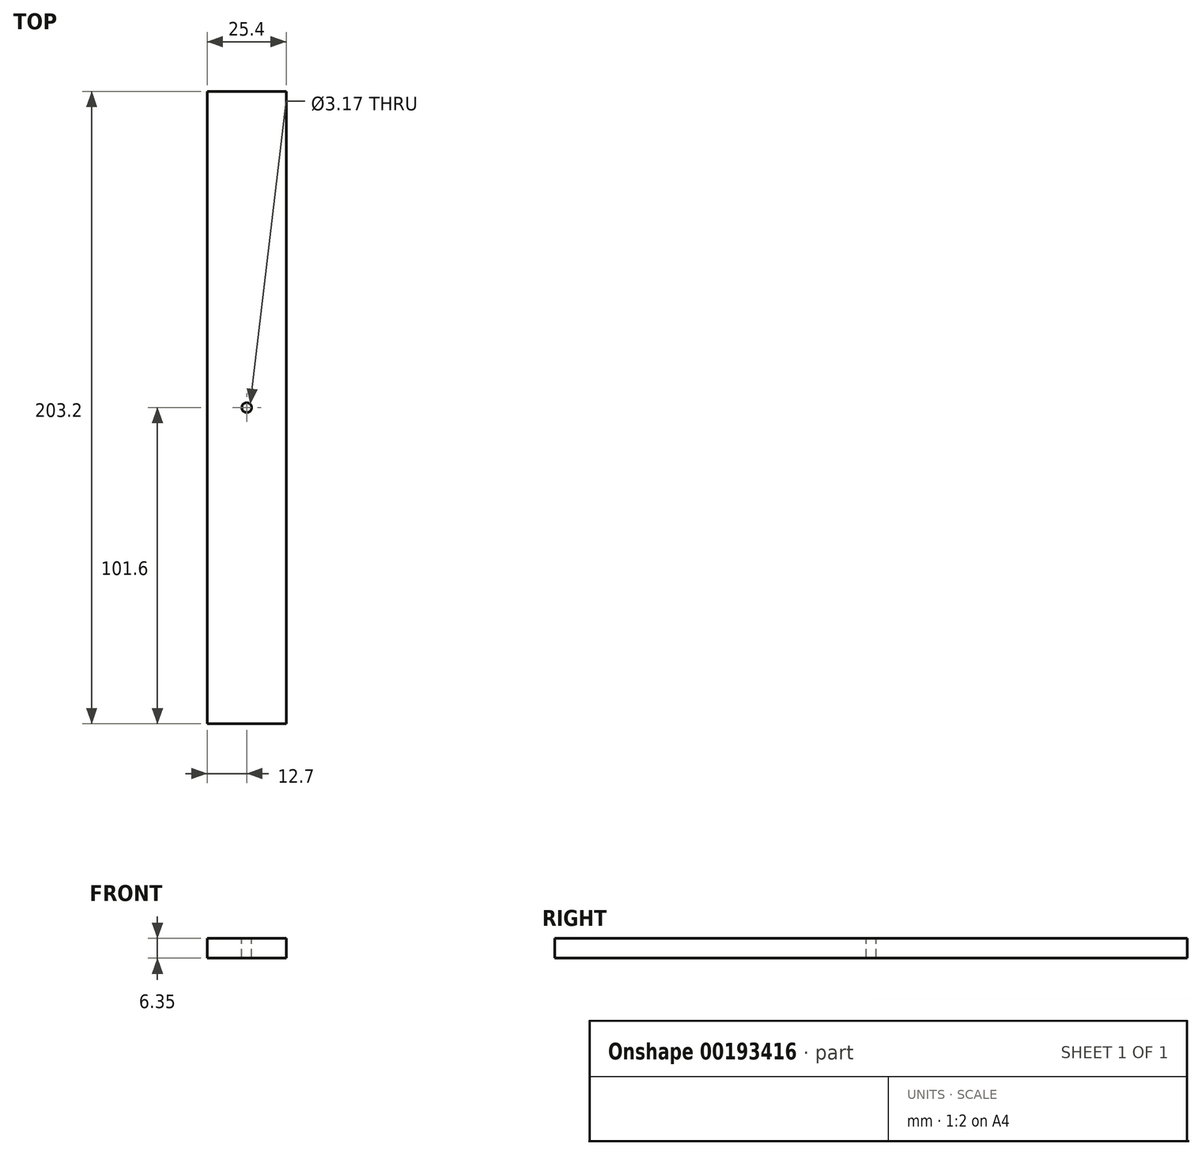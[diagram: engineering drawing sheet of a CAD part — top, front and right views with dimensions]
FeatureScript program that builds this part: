
annotation { "Feature Type Name" : "Feature", "Feature Type Description" : "" }
export const myFeature = defineFeature(function(context is Context, id is Id, definition is map)
    precondition{}
    {
        {
            var Q0;
            Q0=qCreatedBy(makeId("Top.planeOp"),FACE);
            var sketch = newSketch(context, id + "F0", { "sketchPlane" : qUnion([Q0])});
            skLineSegment(sketch, "E0.bottom", {"start": v(12.7, 101.6) * mm, "end": v(-12.7, 101.6) * mm});
            skLineSegment(sketch, "E0.top", {"start": v(12.7, -101.6) * mm, "end": v(-12.7, -101.6) * mm});
            skLineSegment(sketch, "E0.left", {"start": v(12.7, 101.6) * mm, "end": v(12.7, -101.6) * mm});
            skLineSegment(sketch, "E0.right", {"start": v(-12.7, 101.6) * mm, "end": v(-12.7, -101.6) * mm});
            skPoint(sketch, "E0.middle", {"position": v(0, 0) * mm});
            skSolve(sketch);
        }
        {
            var Q0;
            Q0=qSketchRegion(id+"F0",true);
            extrude(context, id + "F1", {"entities" : qUnion([Q0]), "depth" : 6.35 * mm});
        }
        {
            var Q0;
            Q0=makeQuery(id+"F1.opExtrude","CAP_FACE",FACE,{"disambiguationData":[OSD([sQuery(id+"F0.wireOp",EDGE,"E0.bottom"),sQuery(id+"F0.wireOp",EDGE,"E0.top"),sQuery(id+"F0.wireOp",EDGE,"E0.left"),sQuery(id+"F0.wireOp",EDGE,"E0.right")])],"isStart":false});
            var sketch = newSketch(context, id + "F2", { "sketchPlane" : qUnion([Q0])});
            skCircle(sketch, "E1", {"center": v(0, 0) * mm, "radius": 1.59 * mm});
            skSolve(sketch);
        }
        {
            var Q0;
            Q0 = qSketchRegion(id + "F2", true);
            extrude(context, id + "F3", {"entities" : qUnion([Q0]), "operationType" : NewBodyOperationType.REMOVE, "endBound" : BoundingType.THROUGH_ALL, "oppositeDirection" : true, "depth" : 25.4 * mm});
        }
    });
